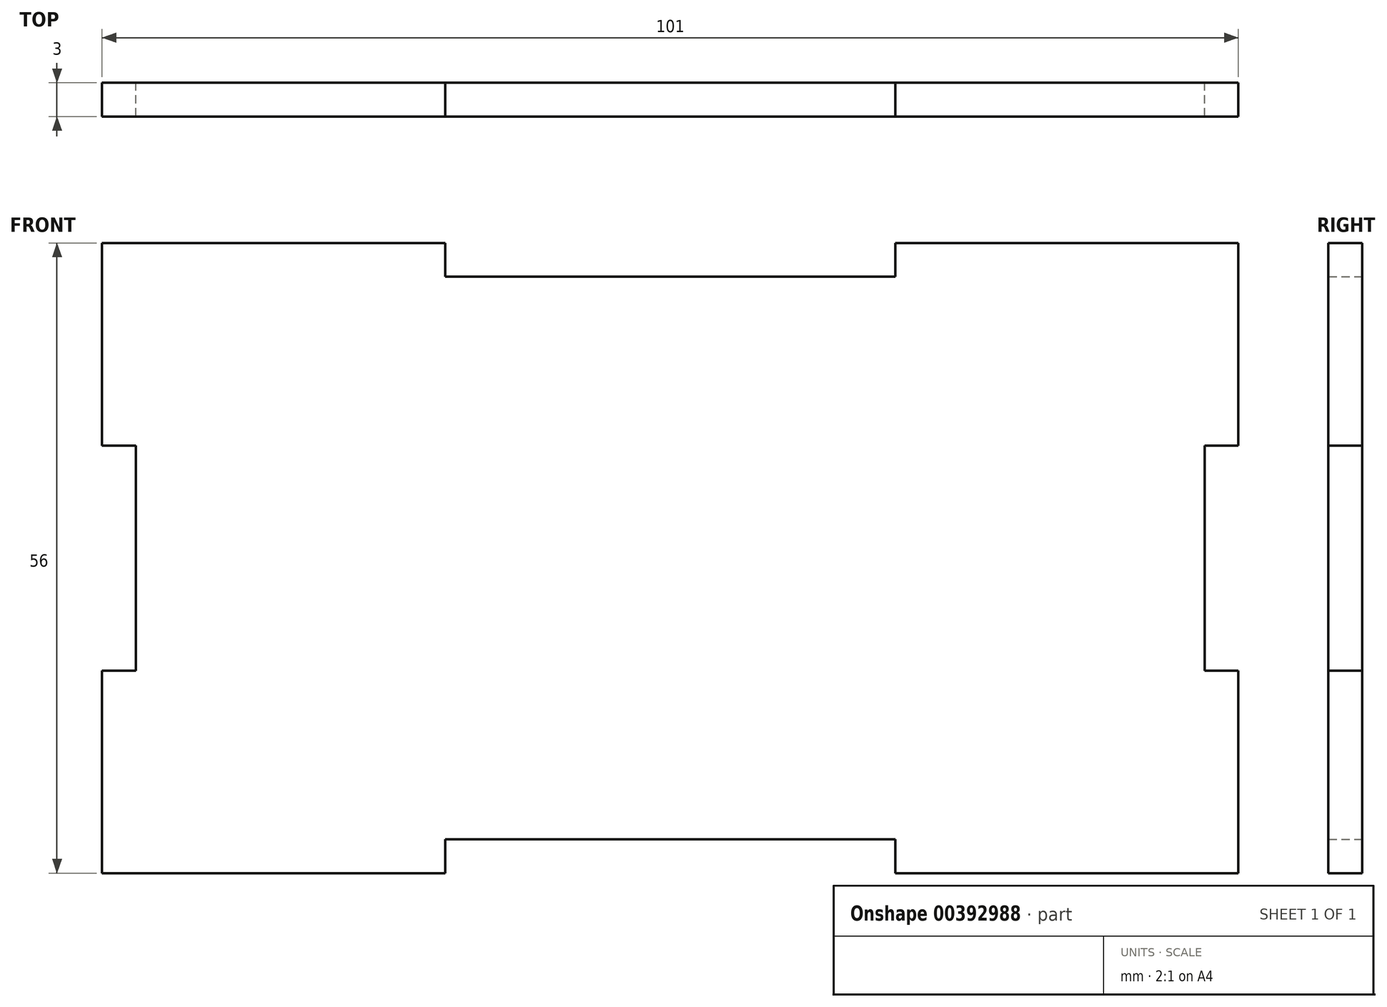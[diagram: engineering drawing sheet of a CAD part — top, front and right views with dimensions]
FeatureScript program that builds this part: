
annotation { "Feature Type Name" : "Feature", "Feature Type Description" : "" }
export const myFeature = defineFeature(function(context is Context, id is Id, definition is map)
    precondition{}
    {
        {
            var Q0;
            Q0=qCreatedBy(makeId("Front.planeOp"),FACE);
            var sketch = newSketch(context, id + "F0", { "sketchPlane" : qUnion([Q0])});
            skLineSegment(sketch, "E0", {"start": v(0, 25) * mm, "end": v(-20, 25) * mm});
            skLineSegment(sketch, "E1", {"start": v(-20, 25) * mm, "end": v(-20, 28) * mm});
            skLineSegment(sketch, "E2", {"start": v(-20, 28) * mm, "end": v(-50.5, 28) * mm});
            skLineSegment(sketch, "E3", {"start": v(-50.5, 28) * mm, "end": v(-50.5, 10) * mm});
            skLineSegment(sketch, "E4", {"start": v(-50.5, 10) * mm, "end": v(-47.5, 10) * mm});
            skLineSegment(sketch, "E5", {"start": v(-47.5, 10) * mm, "end": v(-47.5, 0) * mm});
            skLineSegment(sketch, "E6.MirrorCS", {"start": v(50.5, 10) * mm, "end": v(47.5, 10) * mm});
            skLineSegment(sketch, "E7.MirrorCS", {"start": v(20, 25) * mm, "end": v(20, 28) * mm});
            skLineSegment(sketch, "E8.MirrorCS", {"start": v(47.5, 10) * mm, "end": v(47.5, 0) * mm});
            skLineSegment(sketch, "E9.MirrorCS", {"start": v(0, 25) * mm, "end": v(20, 25) * mm});
            skLineSegment(sketch, "E10.MirrorCS", {"start": v(50.5, 28) * mm, "end": v(50.5, 10) * mm});
            skLineSegment(sketch, "E11.MirrorCS", {"start": v(20, 28) * mm, "end": v(50.5, 28) * mm});
            skLineSegment(sketch, "E12.MirrorCS", {"start": v(20, -25) * mm, "end": v(20, -28) * mm});
            skLineSegment(sketch, "E13.MirrorCS", {"start": v(50.5, -10) * mm, "end": v(47.5, -10) * mm});
            skLineSegment(sketch, "E14.MirrorCS", {"start": v(-20, -25) * mm, "end": v(-20, -28) * mm});
            skLineSegment(sketch, "E15.MirrorCS", {"start": v(-50.5, -10) * mm, "end": v(-47.5, -10) * mm});
            skLineSegment(sketch, "E16.MirrorCS", {"start": v(20, -28) * mm, "end": v(50.5, -28) * mm});
            skLineSegment(sketch, "E17.MirrorCS", {"start": v(50.5, -28) * mm, "end": v(50.5, -10) * mm});
            skLineSegment(sketch, "E18.MirrorCS", {"start": v(0, -25) * mm, "end": v(20, -25) * mm});
            skLineSegment(sketch, "E19.MirrorCS", {"start": v(47.5, -10) * mm, "end": v(47.5, 0) * mm});
            skLineSegment(sketch, "E20.MirrorCS", {"start": v(-20, -28) * mm, "end": v(-50.5, -28) * mm});
            skLineSegment(sketch, "E21.MirrorCS", {"start": v(0, -25) * mm, "end": v(-20, -25) * mm});
            skLineSegment(sketch, "E22.MirrorCS", {"start": v(-47.5, -10) * mm, "end": v(-47.5, 0) * mm});
            skLineSegment(sketch, "E23.MirrorCS", {"start": v(-50.5, -28) * mm, "end": v(-50.5, -10) * mm});
            skSolve(sketch);
        }
        {
            var Q0;
            Q0=qSketchRegion(id+"F0",true);
            extrude(context, id + "F1", {"entities" : qUnion([Q0]), "depth" : 3 * mm});
        }
    });
